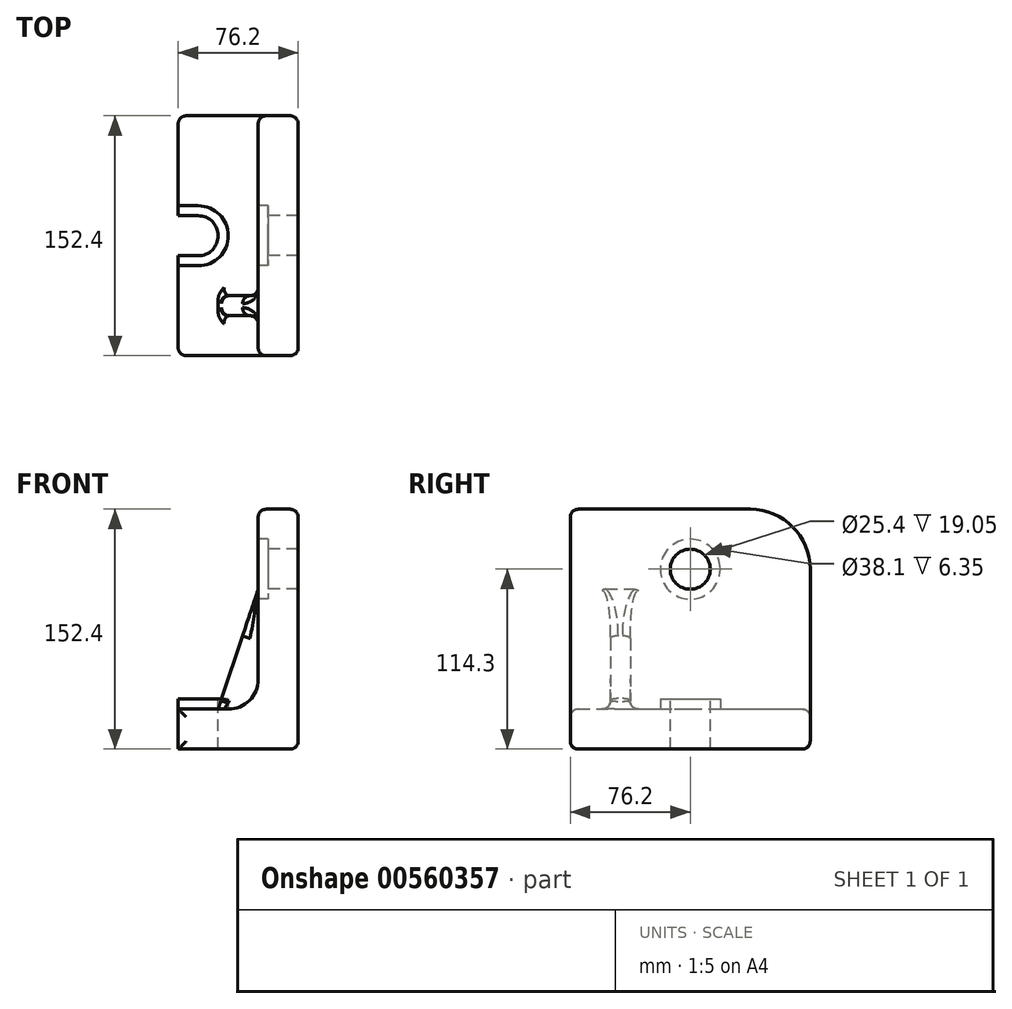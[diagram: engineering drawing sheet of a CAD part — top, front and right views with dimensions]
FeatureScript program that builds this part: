
annotation { "Feature Type Name" : "Feature", "Feature Type Description" : "" }
export const myFeature = defineFeature(function(context is Context, id is Id, definition is map)
    precondition{}
    {
        {
            var Q0;
            Q0=qCreatedBy(makeId("Front.planeOp"),FACE);
            var sketch = newSketch(context, id + "F0", { "sketchPlane" : qUnion([Q0])});
            skLineSegment(sketch, "E0", {"start": v(-76.2, 0) * mm, "end": v(0, 0) * mm});
            skLineSegment(sketch, "E1", {"start": v(0, 0) * mm, "end": v(0, 152.4) * mm});
            skLineSegment(sketch, "E2", {"start": v(0, 152.4) * mm, "end": v(-25.4, 152.4) * mm});
            skLineSegment(sketch, "E3", {"start": v(-25.4, 152.4) * mm, "end": v(-25.4, 25.4) * mm});
            skLineSegment(sketch, "E4", {"start": v(-25.4, 25.4) * mm, "end": v(-76.2, 25.4) * mm});
            skLineSegment(sketch, "E5", {"start": v(-76.2, 25.4) * mm, "end": v(-76.2, 0) * mm});
            skSolve(sketch);
        }
        {
            var Q0;
            Q0=makeQuery(id+"F0.imprint","IMPRINT",FACE,{"disambiguationData":[TD([[makeQuery(id+"F0.imprint","IMPRINT",EDGE,{"derivedFrom":sQuery(id+"F0.wireOp",EDGE,"E0")}),1.0]])]});
            extrude(context, id + "F1", {"entities" : qUnion([Q0]), "endBound" : BoundingType.SYMMETRIC, "depth" : 152.4 * mm, "offsetDistance" : 25.4 * mm});
        }
        {
            var Q0;
            Q0=makeQuery(id+"F1.opExtrude","SWEPT_FACE",FACE,{"disambiguationData":[OSD([sQuery(id+"F0.wireOp",EDGE,"E3")])]});
            var sketch = newSketch(context, id + "F2", { "sketchPlane" : qUnion([Q0])});
            skCircle(sketch, "E6", {"center": v(0, 114.3) * mm, "radius": 12.7 * mm});
            skSolve(sketch);
        }
        {
            var Q0;
            Q0 = qSketchRegion(id + "F2", true);
            extrude(context, id + "F3", {"entities" : qUnion([Q0]), "operationType" : NewBodyOperationType.REMOVE, "endBound" : BoundingType.THROUGH_ALL, "oppositeDirection" : true, "depth" : 25.4 * mm, "offsetDistance" : 25.4 * mm});
        }
        {
            var Q0;
            Q0=makeQuery(id+"F1.opExtrude","SWEPT_FACE",FACE,{"disambiguationData":[OSD([sQuery(id+"F0.wireOp",EDGE,"E4")])]});
            var sketch = newSketch(context, id + "F4", { "sketchPlane" : qUnion([Q0])});
            skLineSegment(sketch, "E7", {"start": v(-76.2, 12.7) * mm, "end": v(-63.5, 12.7) * mm});
            skArc(sketch, "E8", {"start": v(-63.5, 12.7) * mm, "mid": v(-50.8, 0) * mm, "end": v(-63.5, -12.7) * mm});
            skPoint(sketch, "E8.centerSnap0", {"position": v(-25.4, 0) * mm});
            skLineSegment(sketch, "E9", {"start": v(-63.5, -12.7) * mm, "end": v(-76.2, -12.7) * mm});
            skSolve(sketch);
        }
        {
            var Q0;
            {var subQ0=sQuery(id+"F4.wireOp",EDGE,"E7");Q0=makeQuery(id+"F4.imprint","IMPRINT",FACE,{"disambiguationData":[TD([[makeQuery(id+"F4.imprint","IMPRINT",EDGE,{"derivedFrom":subQ0}),-1.0]])]});}
            extrude(context, id + "F5", {"entities" : qUnion([Q0]), "operationType" : NewBodyOperationType.REMOVE, "endBound" : BoundingType.THROUGH_ALL, "oppositeDirection" : true, "depth" : 25.4 * mm, "offsetDistance" : 25.4 * mm});
        }
        {
            var Q0;
            Q0=makeQuery(id+"F1.opExtrude","SWEPT_FACE",FACE,{"disambiguationData":[OSD([sQuery(id+"F0.wireOp",EDGE,"E3")])]});
            var sketch = newSketch(context, id + "F6", { "sketchPlane" : qUnion([Q0])});
            skLineSegment(sketch, "E10.0", {"start": v(-76.2, 152.4) * mm, "end": v(-76.2, 25.4) * mm});
            skLineSegment(sketch, "E10.1", {"start": v(76.2, 152.4) * mm, "end": v(-76.2, 152.4) * mm});
            skArc(sketch, "E11", {"start": v(-38.1, 152.4) * mm, "mid": v(-65.04, 141.24) * mm, "end": v(-76.2, 114.3) * mm});
            skSolve(sketch);
        }
        {
            var Q0;
            {var subQ3=sQuery(id+"F6.wireOp",EDGE,"E11");Q0=makeQuery(id+"F6.imprint","IMPRINT",FACE,{"disambiguationData":[TD([[makeQuery(id+"F6.imprint","IMPRINT",EDGE,{"derivedFrom":subQ3}),-1.0]])]});}
            extrude(context, id + "F7", {"entities" : qUnion([Q0]), "operationType" : NewBodyOperationType.REMOVE, "endBound" : BoundingType.THROUGH_ALL, "oppositeDirection" : true, "depth" : 25.4 * mm, "offsetDistance" : 25.4 * mm});
        }
        {
            var Q0;
            Q0=makeQuery(id+"F1.opExtrude","SWEPT_FACE",FACE,{"disambiguationData":[OSD([sQuery(id+"F0.wireOp",EDGE,"E3")])]});
            var sketch = newSketch(context, id + "F8", { "sketchPlane" : qUnion([Q0])});
            skCircle(sketch, "E12", {"center": v(0, 114.3) * mm, "radius": 19.05 * mm});
            skSolve(sketch);
        }
        {
            var Q0;
            Q0=makeQuery(id+"F8.imprint","IMPRINT",FACE,{"disambiguationData":[TD([[makeQuery(id+"F8.imprint","IMPRINT",EDGE,{"derivedFrom":sQuery(id+"F8.wireOp",EDGE,"E12")}),1.0]])]});
            var Q1;
            Q1=sQuery(id+"F8.wireOp",EDGE,"E12");
            extrude(context, id + "F9", {"entities" : qUnion([Q0]), "operationType" : NewBodyOperationType.REMOVE, "surfaceEntities" : qUnion([Q1]), "oppositeDirection" : true, "depth" : 6.35 * mm, "offsetDistance" : 25.4 * mm});
        }
        {
            var Q0;
            Q0=qCreatedBy(makeId("Front.planeOp"),FACE);
            cPlane(context, id + "F10", {"entities" : qUnion([Q0]), "cplaneType" : CPlaneType.OFFSET, "offset" : 44.45 * mm, "width" : 152.4 * mm, "height" : 152.4 * mm});
        }
        {
            var Q0;
            Q0=qCreatedBy(id+"F10.planeOp",FACE);
            var sketch = newSketch(context, id + "F11", { "sketchPlane" : qUnion([Q0])});
            skLineSegment(sketch, "E13.0", {"start": v(-25.4, 25.4) * mm, "end": v(-76.2, 25.4) * mm});
            skLineSegment(sketch, "E14.0", {"start": v(-25.4, 114.3) * mm, "end": v(-25.4, 25.4) * mm});
            skLineSegment(sketch, "E15.0.0", {"start": v(0, 0) * mm, "end": v(0, 114.3) * mm});
            skLineSegment(sketch, "E15.0.1", {"start": v(0, 114.3) * mm, "end": v(-25.4, 114.3) * mm});
            skLineSegment(sketch, "E15.0.4", {"start": v(-76.2, 25.4) * mm, "end": v(-76.2, 0) * mm});
            skLineSegment(sketch, "E15.0.5", {"start": v(-76.2, 0) * mm, "end": v(0, 0) * mm});
            skLineSegment(sketch, "E16", {"start": v(-25.4, 101.6) * mm, "end": v(-50.8, 25.4) * mm});
            skSolve(sketch);
        }
        {
            var Q0;
            {var subQ3=sQuery(id+"F11.wireOp",EDGE,"E16");Q0=makeQuery(id+"F11.imprint","IMPRINT",FACE,{"disambiguationData":[TD([[makeQuery(id+"F11.imprint","IMPRINT",EDGE,{"derivedFrom":subQ3}),1.0]])]});}
            extrude(context, id + "F12", {"entities" : qUnion([Q0]), "operationType" : NewBodyOperationType.ADD, "endBound" : BoundingType.SYMMETRIC, "depth" : 12.7 * mm, "offsetDistance" : 25.4 * mm});
        }
        {
            var Q0;
            Q0=makeQuery(id+"F1.opExtrude","SWEPT_FACE",FACE,{"disambiguationData":[OSD([sQuery(id+"F0.wireOp",EDGE,"E4")])]});
            var sketch = newSketch(context, id + "F13", { "sketchPlane" : qUnion([Q0])});
            skLineSegment(sketch, "E17.0", {"start": v(-76.2, 12.7) * mm, "end": v(-76.2, 76.2) * mm});
            skLineSegment(sketch, "E17.1", {"start": v(-76.2, 12.7) * mm, "end": v(-63.5, 12.7) * mm});
            skArc(sketch, "E17.2", {"start": v(-63.5, 12.7) * mm, "mid": v(-50.8, 0) * mm, "end": v(-63.5, -12.7) * mm});
            skLineSegment(sketch, "E17.3", {"start": v(-63.5, -12.7) * mm, "end": v(-76.2, -12.7) * mm});
            skLineSegment(sketch, "E17.4", {"start": v(-76.2, -76.2) * mm, "end": v(-76.2, -12.7) * mm});
            skLineSegment(sketch, "E18.0", {"start": v(-63.5, -19.05) * mm, "end": v(-76.2, -19.05) * mm});
            skArc(sketch, "E18.1", {"start": v(-63.5, 19.05) * mm, "mid": v(-44.45, 0) * mm, "end": v(-63.5, -19.05) * mm});
            skLineSegment(sketch, "E18.2", {"start": v(-76.2, 19.05) * mm, "end": v(-63.5, 19.05) * mm});
            skSolve(sketch);
        }
        {
            var Q0;
            {var subQ1=sQuery(id+"F13.wireOp",EDGE,"E17.1");Q0=makeQuery(id+"F13.imprint","IMPRINT",FACE,{"disambiguationData":[TD([[makeQuery(id+"F13.imprint","IMPRINT",EDGE,{"derivedFrom":subQ1}),1.0]])]});}
            extrude(context, id + "F14", {"entities" : qUnion([Q0]), "operationType" : NewBodyOperationType.ADD, "depth" : 6.35 * mm, "offsetDistance" : 25.4 * mm});
        }
        {
            var Q0;
            {var subQ0=sQuery(id+"F0.wireOp",EDGE,"E4");var subQ1=sQuery(id+"F0.wireOp",EDGE,"E3");var subQ4=sQuery(id+"F11.wireOp",EDGE,"E16");var subQ5=sQuery(id+"F11.wireOp",EDGE,"E13.0");var subQ6=sQuery(id+"F11.wireOp",EDGE,"E14.0");Q0=makeQuery(id+"FUIa0YllPn415Zh_1.1.F12.boolean.opBoolean","SPLIT",EDGE,{"disambiguationData":[TD([makeQuery(id+"FUIa0YllPn415Zh_1.1.F12.opExtrude","CAP_FACE",FACE,{"disambiguationData":[OSD([subQ6,subQ5,subQ4])],"isStart":false})])],"derivedFrom":makeQuery(id+"F12.boolean.opBoolean","SPLIT",EDGE,{"disambiguationData":[TD([makeQuery(id+"F12.opExtrude","CAP_FACE",FACE,{"disambiguationData":[OSD([subQ6,subQ5,subQ4])],"isStart":true})])],"derivedFrom":makeQuery(id+"F1.opExtrude","SWEPT_EDGE",EDGE,{"disambiguationData":[OSD([subQ1,subQ0])]})})});}
            var Q1;
            {var subQ0=sQuery(id+"F0.wireOp",EDGE,"E3");var subQ2=sQuery(id+"F11.wireOp",EDGE,"E16");var subQ3=sQuery(id+"F11.wireOp",EDGE,"E13.0");var subQ4=sQuery(id+"F11.wireOp",EDGE,"E14.0");var subQ5=sQuery(id+"F0.wireOp",EDGE,"E4");var subQ7=makeQuery(id+"F12.opExtrude","CAP_FACE",FACE,{"disambiguationData":[OSD([subQ4,subQ3,subQ2])],"isStart":true});Q1=makeQuery(id+"FUIa0YllPn415Zh_1.1.F12.boolean.opBoolean","SPLIT",EDGE,{"disambiguationData":[TD([subQ7])],"derivedFrom":makeQuery(id+"F12.boolean.opBoolean","SPLIT",EDGE,{"disambiguationData":[TD([subQ7])],"derivedFrom":makeQuery(id+"F1.opExtrude","SWEPT_EDGE",EDGE,{"disambiguationData":[OSD([subQ0,subQ5])]})})});}
            var Q2;
            {var subQ0=sQuery(id+"F0.wireOp",EDGE,"E4");var subQ1=sQuery(id+"F0.wireOp",EDGE,"E3");Q2=makeQuery(id+"F12.boolean.opBoolean","SPLIT",EDGE,{"disambiguationData":[TD([makeQuery(id+"F12.opExtrude","CAP_FACE",FACE,{"disambiguationData":[OSD([sQuery(id+"F11.wireOp",EDGE,"E14.0"),sQuery(id+"F11.wireOp",EDGE,"E13.0"),sQuery(id+"F11.wireOp",EDGE,"E16")])],"isStart":false})])],"derivedFrom":makeQuery(id+"F1.opExtrude","SWEPT_EDGE",EDGE,{"disambiguationData":[OSD([subQ1,subQ0])]})});}
            fillet(context, id + "F15", {"entities" : qUnion([Q0, Q1, Q2]), "radius" : 19.05 * mm, "tangentPropagation" : true, "allowEdgeOverflow" : false});
        }
        {
            var Q0;
            Q0=makeQuery(id+"F1.opExtrude","CAP_EDGE",EDGE,{"disambiguationData":[OSD([sQuery(id+"F0.wireOp",EDGE,"E4")])],"isStart":false});
            var Q1;
            Q1=makeQuery(id+"F1.opExtrude","CAP_EDGE",EDGE,{"disambiguationData":[OSD([sQuery(id+"F0.wireOp",EDGE,"E3")])],"isStart":false});
            var Q2;
            Q2=makeQuery(id+"F1.opExtrude","CAP_EDGE",EDGE,{"disambiguationData":[OSD([sQuery(id+"F0.wireOp",EDGE,"E4")])],"isStart":true});
            var Q3;
            Q3=makeQuery(id+"F1.opExtrude","CAP_FACE",FACE,{"disambiguationData":[OSD([sQuery(id+"F0.wireOp",EDGE,"E0"),sQuery(id+"F0.wireOp",EDGE,"E1"),sQuery(id+"F0.wireOp",EDGE,"E2"),sQuery(id+"F0.wireOp",EDGE,"E3"),sQuery(id+"F0.wireOp",EDGE,"E4"),sQuery(id+"F0.wireOp",EDGE,"E5")])],"isStart":true});
            var Q4;
            Q4=makeQuery(id+"F1.opExtrude","SWEPT_EDGE",EDGE,{"disambiguationData":[OSD([sQuery(id+"F0.wireOp",EDGE,"E0"),sQuery(id+"F0.wireOp",EDGE,"E1")])]});
            var Q5;
            Q5=makeQuery(id+"F1.opExtrude","CAP_FACE",FACE,{"disambiguationData":[OSD([sQuery(id+"F0.wireOp",EDGE,"E0"),sQuery(id+"F0.wireOp",EDGE,"E1"),sQuery(id+"F0.wireOp",EDGE,"E2"),sQuery(id+"F0.wireOp",EDGE,"E3"),sQuery(id+"F0.wireOp",EDGE,"E4"),sQuery(id+"F0.wireOp",EDGE,"E5")])],"isStart":false});
            fillet(context, id + "F16", {"entities" : qUnion([Q0, Q1, Q2, Q3, Q4, Q5]), "radius" : 5.08 * mm, "tangentPropagation" : true, "allowEdgeOverflow" : false});
        }
        {
            var Q0;
            {var subQ0=makeQuery(id+"F12.opExtrude","CAP_FACE",FACE,{"disambiguationData":[OSD([sQuery(id+"F11.wireOp",EDGE,"E14.0"),sQuery(id+"F11.wireOp",EDGE,"E13.0"),sQuery(id+"F11.wireOp",EDGE,"E16")])],"isStart":false});var subQ1=sQuery(id+"F0.wireOp",EDGE,"E4");var subQ2=sQuery(id+"F0.wireOp",EDGE,"E3");Q0=makeQuery(id+"F15.opFillet","BLEND_EDGE",EDGE,{"blendedFrom":[makeQuery(id+"F12.boolean.opBoolean","SPLIT",EDGE,{"disambiguationData":[TD([subQ0])],"derivedFrom":makeQuery(id+"F1.opExtrude","SWEPT_EDGE",EDGE,{"disambiguationData":[OSD([subQ2,subQ1])]})}),subQ0],"blendedInto":[subQ0]});}
            var Q1;
            Q1=makeQuery(id+"F12.opExtrude","CAP_EDGE",EDGE,{"disambiguationData":[OSD([sQuery(id+"F11.wireOp",EDGE,"E13.0")])],"isStart":false});
            var Q2;
            Q2=makeQuery(id+"F12.opExtrude","SWEPT_EDGE",EDGE,{"disambiguationData":[OSD([sQuery(id+"F11.wireOp",EDGE,"E13.0"),sQuery(id+"F11.wireOp",EDGE,"E16")])]});
            var Q3;
            Q3=makeQuery(id+"F12.opExtrude","CAP_EDGE",EDGE,{"disambiguationData":[OSD([sQuery(id+"F11.wireOp",EDGE,"E13.0")])],"isStart":true});
            var Q4;
            {var subQ0=sQuery(id+"F11.wireOp",EDGE,"E16");var subQ1=sQuery(id+"F11.wireOp",EDGE,"E13.0");var subQ2=sQuery(id+"F11.wireOp",EDGE,"E14.0");var subQ3=makeQuery(id+"F12.opExtrude","CAP_FACE",FACE,{"disambiguationData":[OSD([subQ2,subQ1,subQ0])],"isStart":true});var subQ4=sQuery(id+"F0.wireOp",EDGE,"E3");var subQ6=sQuery(id+"F0.wireOp",EDGE,"E4");Q4=makeQuery(id+"F15.opFillet","BLEND_EDGE",EDGE,{"blendedFrom":[makeQuery(id+"FUIa0YllPn415Zh_1.1.F12.boolean.opBoolean","SPLIT",EDGE,{"disambiguationData":[TD([subQ3])],"derivedFrom":makeQuery(id+"F12.boolean.opBoolean","SPLIT",EDGE,{"disambiguationData":[TD([subQ3])],"derivedFrom":makeQuery(id+"F1.opExtrude","SWEPT_EDGE",EDGE,{"disambiguationData":[OSD([subQ4,subQ6])]})})}),subQ3],"blendedInto":[subQ3]});}
            var Q5;
            Q5=makeQuery(id+"F12.opExtrude","CAP_EDGE",EDGE,{"disambiguationData":[OSD([sQuery(id+"F11.wireOp",EDGE,"E14.0")])],"isStart":false});
            var Q6;
            Q6=makeQuery(id+"F12.opExtrude","CAP_EDGE",EDGE,{"disambiguationData":[OSD([sQuery(id+"F11.wireOp",EDGE,"E14.0")])],"isStart":true});
            var Q7;
            Q7=makeQuery(id+"F12.opExtrude","SWEPT_EDGE",EDGE,{"disambiguationData":[OSD([sQuery(id+"F11.wireOp",EDGE,"E14.0"),sQuery(id+"F11.wireOp",EDGE,"E16")])]});
            var Q8;
            {var subQ0=sQuery(id+"F11.wireOp",EDGE,"E16");var subQ1=sQuery(id+"F11.wireOp",EDGE,"E13.0");var subQ2=sQuery(id+"F11.wireOp",EDGE,"E14.0");var subQ3=makeQuery(id+"FUIa0YllPn415Zh_1.1.F12.opExtrude","CAP_FACE",FACE,{"disambiguationData":[OSD([subQ2,subQ1,subQ0])],"isStart":false});var subQ4=sQuery(id+"F0.wireOp",EDGE,"E4");var subQ5=sQuery(id+"F0.wireOp",EDGE,"E3");Q8=makeQuery(id+"F15.opFillet","BLEND_EDGE",EDGE,{"blendedFrom":[makeQuery(id+"FUIa0YllPn415Zh_1.1.F12.boolean.opBoolean","SPLIT",EDGE,{"disambiguationData":[TD([subQ3])],"derivedFrom":makeQuery(id+"F12.boolean.opBoolean","SPLIT",EDGE,{"disambiguationData":[TD([makeQuery(id+"F12.opExtrude","CAP_FACE",FACE,{"disambiguationData":[OSD([subQ2,subQ1,subQ0])],"isStart":true})])],"derivedFrom":makeQuery(id+"F1.opExtrude","SWEPT_EDGE",EDGE,{"disambiguationData":[OSD([subQ5,subQ4])]})})}),subQ3],"blendedInto":[subQ3]});}
            var Q9;
            Q9=makeQuery(id+"FUIa0YllPn415Zh_1.1.F12.opExtrude","CAP_EDGE",EDGE,{"disambiguationData":[OSD([sQuery(id+"F11.wireOp",EDGE,"E13.0")])],"isStart":false});
            var Q10;
            Q10=makeQuery(id+"FUIa0YllPn415Zh_1.1.F12.opExtrude","SWEPT_EDGE",EDGE,{"disambiguationData":[OSD([sQuery(id+"F11.wireOp",EDGE,"E13.0"),sQuery(id+"F11.wireOp",EDGE,"E16")])]});
            var Q11;
            {var subQ0=sQuery(id+"F11.wireOp",EDGE,"E16");var subQ1=sQuery(id+"F11.wireOp",EDGE,"E13.0");var subQ2=sQuery(id+"F11.wireOp",EDGE,"E14.0");var subQ3=makeQuery(id+"FUIa0YllPn415Zh_1.1.F12.opExtrude","CAP_FACE",FACE,{"disambiguationData":[OSD([subQ2,subQ1,subQ0])],"isStart":true});var subQ4=sQuery(id+"F0.wireOp",EDGE,"E3");var subQ6=sQuery(id+"F0.wireOp",EDGE,"E4");var subQ8=makeQuery(id+"F12.opExtrude","CAP_FACE",FACE,{"disambiguationData":[OSD([subQ2,subQ1,subQ0])],"isStart":true});Q11=makeQuery(id+"F15.opFillet","BLEND_EDGE",EDGE,{"blendedFrom":[makeQuery(id+"FUIa0YllPn415Zh_1.1.F12.boolean.opBoolean","SPLIT",EDGE,{"disambiguationData":[TD([subQ8])],"derivedFrom":makeQuery(id+"F12.boolean.opBoolean","SPLIT",EDGE,{"disambiguationData":[TD([subQ8])],"derivedFrom":makeQuery(id+"F1.opExtrude","SWEPT_EDGE",EDGE,{"disambiguationData":[OSD([subQ4,subQ6])]})})}),subQ3],"blendedInto":[subQ3]});}
            var Q12;
            Q12=makeQuery(id+"FUIa0YllPn415Zh_1.1.F12.opExtrude","CAP_EDGE",EDGE,{"disambiguationData":[OSD([sQuery(id+"F11.wireOp",EDGE,"E14.0")])],"isStart":true});
            var Q13;
            Q13=makeQuery(id+"FUIa0YllPn415Zh_1.1.F12.opExtrude","SWEPT_EDGE",EDGE,{"disambiguationData":[OSD([sQuery(id+"F11.wireOp",EDGE,"E14.0"),sQuery(id+"F11.wireOp",EDGE,"E16")])]});
            var Q14;
            Q14=makeQuery(id+"FUIa0YllPn415Zh_1.1.F12.opExtrude","CAP_EDGE",EDGE,{"disambiguationData":[OSD([sQuery(id+"F11.wireOp",EDGE,"E14.0")])],"isStart":false});
            fillet(context, id + "F17", {"entities" : qUnion([Q0, Q1, Q2, Q3, Q4, Q5, Q6, Q7, Q8, Q9, Q10, Q11, Q12, Q13, Q14]), "radius" : 5.08 * mm, "tangentPropagation" : true, "allowEdgeOverflow" : false});
        }
        {
            var Q0;
            Q0=makeQuery(id+"F12.opExtrude","CAP_EDGE",EDGE,{"disambiguationData":[OSD([sQuery(id+"F11.wireOp",EDGE,"E16")])],"isStart":false});
            var Q1;
            Q1=makeQuery(id+"F12.opExtrude","CAP_EDGE",EDGE,{"disambiguationData":[OSD([sQuery(id+"F11.wireOp",EDGE,"E16")])],"isStart":true});
            fillet(context, id + "F18", {"entities" : qUnion([Q0, Q1]), "radius" : 5.08 * mm, "tangentPropagation" : true, "allowEdgeOverflow" : false});
        }
    });
